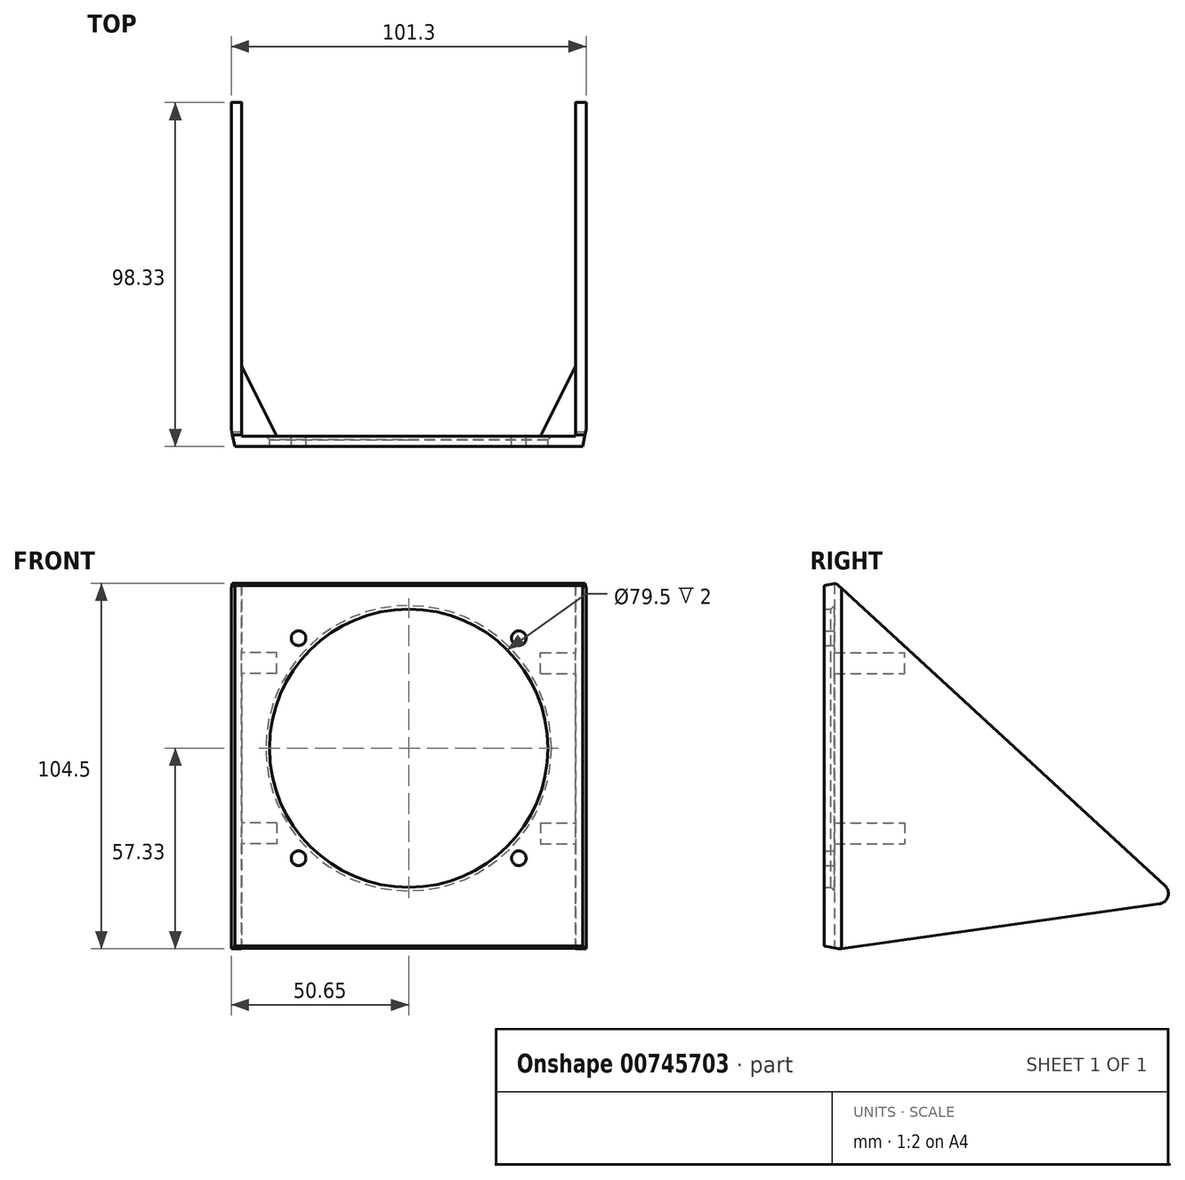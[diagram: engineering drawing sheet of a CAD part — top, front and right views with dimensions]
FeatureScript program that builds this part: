
annotation { "Feature Type Name" : "Feature", "Feature Type Description" : "" }
export const myFeature = defineFeature(function(context is Context, id is Id, definition is map)
    precondition{}
    {
        {
            var Q0;
            Q0=qCreatedBy(makeId("Front.planeOp"),FACE);
            var sketch = newSketch(context, id + "F0", { "sketchPlane" : qUnion([Q0])});
            skLineSegment(sketch, "E0.bottom", {"start": v(-50.65, 47.5) * mm, "end": v(50.65, 47.5) * mm});
            skLineSegment(sketch, "E0.top", {"start": v(-50.65, -57.5) * mm, "end": v(50.65, -57.5) * mm});
            skLineSegment(sketch, "E0.left", {"start": v(-50.65, 47.5) * mm, "end": v(-50.65, -57.5) * mm});
            skLineSegment(sketch, "E0.right", {"start": v(50.65, 47.5) * mm, "end": v(50.65, -57.5) * mm});
            skCircle(sketch, "E1", {"center": v(0, 0) * mm, "radius": 39.75 * mm});
            skLineSegment(sketch, "E2", {"start": v(0, 47.5) * mm, "end": v(0, -57.5) * mm, "construction": true});
            skLineSegment(sketch, "E3", {"start": v(-50.65, 0) * mm, "end": v(56.31, 0) * mm, "construction": true});
            skCircle(sketch, "E4", {"center": v(-31.45, 31.45) * mm, "radius": 2.1 * mm});
            skCircle(sketch, "E5.MirrorC", {"center": v(-31.45, -31.45) * mm, "radius": 2.1 * mm});
            skCircle(sketch, "E6.MirrorC", {"center": v(31.45, 31.45) * mm, "radius": 2.1 * mm});
            skCircle(sketch, "E7.MirrorC", {"center": v(31.45, -31.45) * mm, "radius": 2.1 * mm});
            skSolve(sketch);
        }
        {
            var Q0;
            Q0=qCreatedBy(makeId("Right.planeOp"),FACE);
            var Q1;
            Q1=sQuery(id+"F0.wireOp",VERTEX,"E0.right.start");
            cPlane(context, id + "F1", {"entities" : qUnion([Q0, Q1]), "cplaneType" : CPlaneType.PLANE_POINT, "offset" : 25 * mm, "width" : 150 * mm, "height" : 150 * mm});
        }
        {
            var Q0;
            Q0=qCreatedBy(id+"F1.planeOp",FACE);
            var sketch = newSketch(context, id + "F2", { "sketchPlane" : qUnion([Q0])});
            skLineSegment(sketch, "E8", {"start": v(0, -57.5) * mm, "end": v(92.74, -44.47) * mm});
            skLineSegment(sketch, "E9", {"start": v(94.36, -39.29) * mm, "end": v(0, 47.5) * mm});
            skPoint(sketch, "E10.visualSharp", {"position": v(99.03, -43.58) * mm});
            skArc(sketch, "E10.filletArc", {"start": v(92.74, -44.47) * mm, "mid": v(95.19, -42.39) * mm, "end": v(94.36, -39.29) * mm});
            skLineSegment(sketch, "E11", {"start": v(0, 47.5) * mm, "end": v(0, -57.5) * mm});
            skSolve(sketch);
        }
        {
            var Q0;
            Q0 = qSketchRegion(id + "F0", true);
            extrude(context, id + "F3", {"entities" : qUnion([Q0]), "depth" : 3 * mm, "offsetDistance" : 25 * mm});
        }
        {
            var Q0;
            Q0=makeQuery(id+"F2.imprint","IMPRINT",FACE,{"disambiguationData":[TD([[makeQuery(id+"F2.imprint","IMPRINT",EDGE,{"derivedFrom":sQuery(id+"F2.wireOp",EDGE,"E8")}),1.0]])]});
            extrude(context, id + "F4", {"entities" : qUnion([Q0]), "oppositeDirection" : true, "depth" : 3 * mm, "offsetDistance" : 25 * mm});
        }
        {
            var Q0;
            Q0=makeQuery(id+"F4.opExtrude","SWEPT_BODY",BODY,{"disambiguationData":[OSD([sQuery(id+"F2.wireOp",EDGE,"E8"),sQuery(id+"F2.wireOp",EDGE,"E9"),sQuery(id+"F2.wireOp",EDGE,"E10.filletArc"),sQuery(id+"F2.wireOp",EDGE,"E11")])]});
            var Q1;
            Q1=qCreatedBy(makeId("Right.planeOp"),FACE);
            mirror(context, id + "F5", {"operationType" : NewBodyOperationType.ADD, "entities" : qUnion([Q0]), "mirrorPlane" : qUnion([Q1])});
        }
        {
            var Q0;
            Q0=makeQuery(id+"F3.opExtrude","CAP_EDGE",EDGE,{"disambiguationData":[OSD([sQuery(id+"F0.wireOp",EDGE,"E0.bottom")])],"isStart":false});
            chamfer(context, id + "F6", {"entities" : qUnion([Q0]), "chamferType" : ChamferType.TWO_OFFSETS, "width1" : 5 * mm, "oppositeDirection" : false, "width2" : 1 * mm, "tangentPropagation" : true});
        }
        {
            var Q0;
            Q0=makeQuery(id+"F3.opExtrude","CAP_EDGE",EDGE,{"disambiguationData":[OSD([sQuery(id+"F0.wireOp",EDGE,"E0.right")])],"isStart":false});
            chamfer(context, id + "F7", {"entities" : qUnion([Q0]), "chamferType" : ChamferType.TWO_OFFSETS, "width1" : 5 * mm, "oppositeDirection" : false, "width2" : 1 * mm, "tangentPropagation" : true});
        }
        {
            var Q0;
            Q0=makeQuery(id+"F3.opExtrude","CAP_EDGE",EDGE,{"disambiguationData":[OSD([sQuery(id+"F0.wireOp",EDGE,"E0.left")])],"isStart":false});
            chamfer(context, id + "F8", {"entities" : qUnion([Q0]), "chamferType" : ChamferType.TWO_OFFSETS, "width1" : 1 * mm, "oppositeDirection" : false, "width2" : 5 * mm, "tangentPropagation" : true});
        }
        {
            var Q0;
            Q0=makeQuery(id+"F3.opExtrude","CAP_EDGE",EDGE,{"disambiguationData":[OSD([sQuery(id+"F0.wireOp",EDGE,"E0.top")])],"isStart":false});
            chamfer(context, id + "F9", {"entities" : qUnion([Q0]), "chamferType" : ChamferType.TWO_OFFSETS, "width1" : 1 * mm, "oppositeDirection" : false, "width2" : 5 * mm, "tangentPropagation" : true});
        }
        {
            var Q0;
            Q0=makeQuery(id+"F3.opExtrude","CAP_EDGE",EDGE,{"disambiguationData":[OSD([sQuery(id+"F0.wireOp",EDGE,"E1")])],"isStart":true});
            chamfer(context, id + "F10", {"entities" : qUnion([Q0]), "width" : 1 * mm, "tangentPropagation" : true});
        }
        {
            var Q0;
            Q0=qCreatedBy(makeId("Top.planeOp"),FACE);
            cPlane(context, id + "F11", {"entities" : qUnion([Q0]), "cplaneType" : CPlaneType.OFFSET, "offset" : 27.3 * mm, "oppositeDirection" : true, "width" : 150 * mm, "height" : 150 * mm});
        }
        {
            var Q0;
            Q0=qCreatedBy(id+"F11.planeOp",FACE);
            var sketch = newSketch(context, id + "F12", { "sketchPlane" : qUnion([Q0])});
            skLineSegment(sketch, "E12", {"start": v(-37.65, 0) * mm, "end": v(-47.65, 0) * mm});
            skLineSegment(sketch, "E13", {"start": v(-47.65, 0) * mm, "end": v(-47.65, 20) * mm});
            skLineSegment(sketch, "E14", {"start": v(-47.65, 20) * mm, "end": v(-37.65, 0) * mm});
            skLineSegment(sketch, "E15", {"start": v(0, -14.19) * mm, "end": v(0, 17.13) * mm, "construction": true});
            skLineSegment(sketch, "E16.MirrorCS", {"start": v(47.65, 20) * mm, "end": v(37.65, 0) * mm});
            skLineSegment(sketch, "E17.MirrorCS", {"start": v(37.65, 0) * mm, "end": v(47.65, 0) * mm});
            skLineSegment(sketch, "E18.MirrorCS", {"start": v(47.65, 0) * mm, "end": v(47.65, 20) * mm});
            skSolve(sketch);
        }
        {
            var Q0;
            Q0 = qSketchRegion(id + "F12", true);
            extrude(context, id + "F13", {"entities" : qUnion([Q0]), "depth" : 6 * mm, "offsetDistance" : 25 * mm});
        }
        {
            var Q0;
            Q0=makeQuery(id+"F13.opExtrude","SWEPT_BODY",BODY,{"disambiguationData":[OSD([sQuery(id+"F12.wireOp",EDGE,"E16.MirrorCS"),sQuery(id+"F12.wireOp",EDGE,"E17.MirrorCS"),sQuery(id+"F12.wireOp",EDGE,"E18.MirrorCS")])]});
            var Q1;
            Q1=makeQuery(id+"F13.opExtrude","SWEPT_BODY",BODY,{"disambiguationData":[OSD([sQuery(id+"F12.wireOp",EDGE,"E12"),sQuery(id+"F12.wireOp",EDGE,"E13"),sQuery(id+"F12.wireOp",EDGE,"E14")])]});
            var Q2;
            Q2=qCreatedBy(makeId("Top.planeOp"),FACE);
            mirror(context, id + "F14", {"operationType" : NewBodyOperationType.ADD, "entities" : qUnion([Q0, Q1]), "mirrorPlane" : qUnion([Q2])});
        }
    });
